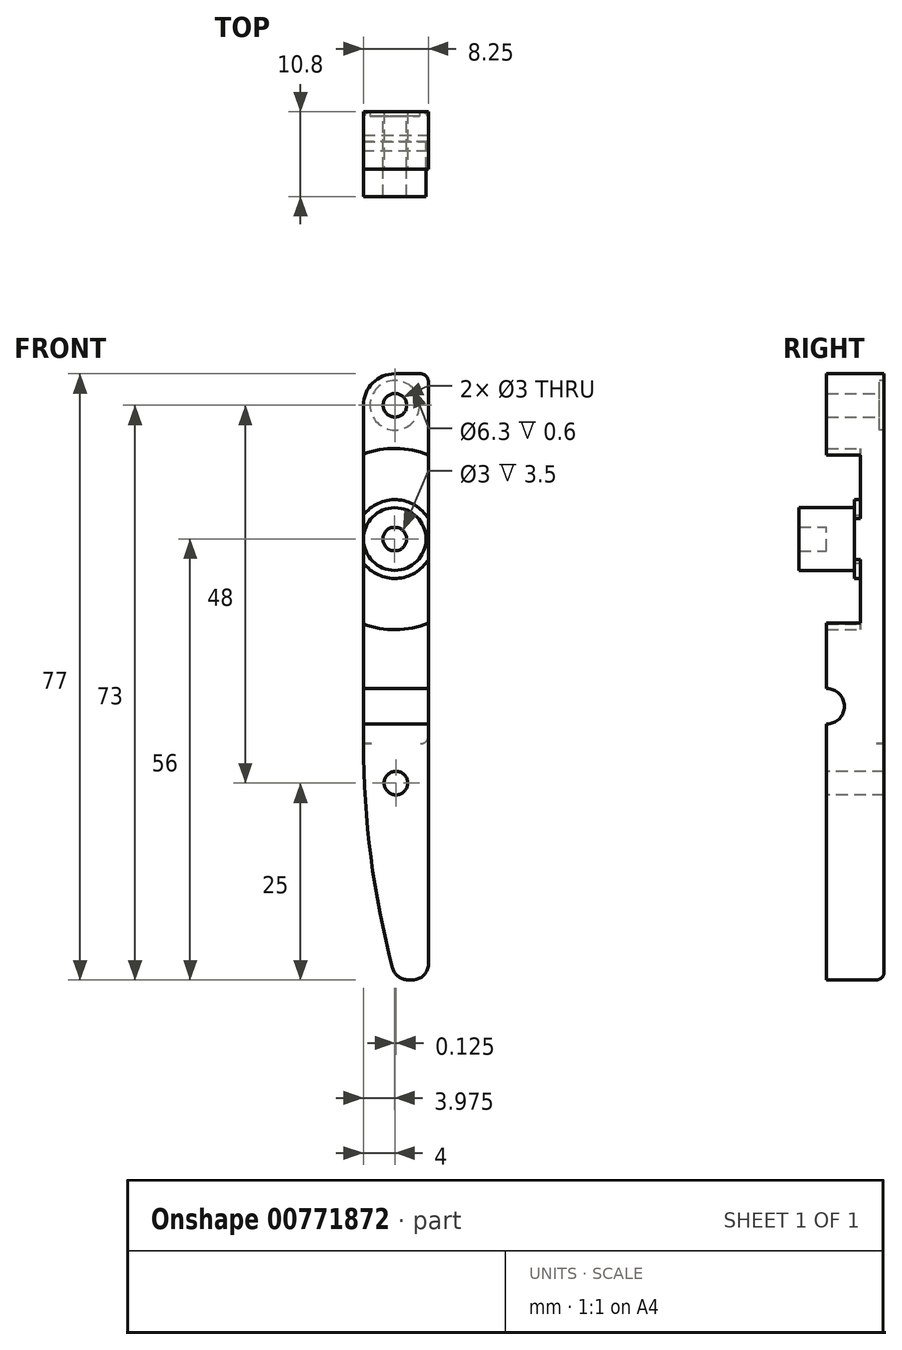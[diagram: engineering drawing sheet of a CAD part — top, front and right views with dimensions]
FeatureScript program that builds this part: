
annotation { "Feature Type Name" : "Feature", "Feature Type Description" : "" }
export const myFeature = defineFeature(function(context is Context, id is Id, definition is map)
    precondition{}
    {
        {
            var Q0;
            Q0=qCreatedBy(makeId("Front.planeOp"),FACE);
            var sketch = newSketch(context, id + "F0", { "sketchPlane" : qUnion([Q0])});
            skLineSegment(sketch, "E0.top", {"start": v(4, 47) * mm, "end": v(8.25, 47) * mm});
            skLineSegment(sketch, "E0.left", {"start": v(0, 0) * mm, "end": v(0, 43) * mm});
            skLineSegment(sketch, "E0.right", {"start": v(8.25, -28) * mm, "end": v(8.25, 47) * mm});
            skCircle(sketch, "E1", {"center": v(4, 43) * mm, "radius": 1.5 * mm});
            skPoint(sketch, "E2.visualSharp", {"position": v(0, 47) * mm});
            skArc(sketch, "E2.filletArc", {"start": v(4, 47) * mm, "mid": v(1.17, 45.83) * mm, "end": v(0, 43) * mm});
            skCircle(sketch, "E3", {"center": v(3.98, 26) * mm, "radius": 3.98 * mm});
            skArc(sketch, "E4", {"start": v(8.25, 28.6) * mm, "mid": v(4.24, 31) * mm, "end": v(0, 29.03) * mm});
            skArc(sketch, "E5.trimOffspring", {"start": v(0, 22.97) * mm, "mid": v(4.24, 21) * mm, "end": v(8.25, 23.4) * mm});
            skArc(sketch, "E6", {"start": v(0, 0) * mm, "mid": v(0.93, -14.38) * mm, "end": v(3.72, -28.51) * mm});
            skLineSegment(sketch, "E7", {"start": v(6.25, -30) * mm, "end": v(5.65, -30) * mm});
            skPoint(sketch, "E8.visualSharp", {"position": v(4.13, -30) * mm});
            skArc(sketch, "E8.filletArc", {"start": v(3.72, -28.51) * mm, "mid": v(4.43, -29.59) * mm, "end": v(5.65, -30) * mm});
            skPoint(sketch, "E9.visualSharp", {"position": v(8.25, -30) * mm});
            skArc(sketch, "E9.filletArc", {"start": v(6.25, -30) * mm, "mid": v(7.66, -29.41) * mm, "end": v(8.25, -28) * mm});
            skArc(sketch, "E10", {"start": v(8.25, 36.68) * mm, "mid": v(4.14, 37.5) * mm, "end": v(0, 36.8) * mm});
            skArc(sketch, "E11.trimOffspring", {"start": v(0, 15.2) * mm, "mid": v(4.14, 14.5) * mm, "end": v(8.25, 15.32) * mm});
            skLineSegment(sketch, "E12", {"start": v(8.25, 26) * mm, "end": v(7.95, 26) * mm});
            skCircle(sketch, "E13", {"center": v(3.98, 26) * mm, "radius": 1.5 * mm});
            skLineSegment(sketch, "E14", {"start": v(0, 0) * mm, "end": v(8.25, 0) * mm});
            skCircle(sketch, "E15", {"center": v(4.13, -5) * mm, "radius": 1.5 * mm});
            skPoint(sketch, "E16", {"position": v(4.13, 0) * mm});
            skCircle(sketch, "E17", {"center": v(4, 43) * mm, "radius": 3.15 * mm});
            skSolve(sketch);
        }
        {
            var Q0;
            Q0=qCreatedBy(makeId("Right.planeOp"),FACE);
            var sketch = newSketch(context, id + "F1", { "sketchPlane" : qUnion([Q0])});
            skCircle(sketch, "E18", {"center": v(-4.3, 4.75) * mm, "radius": 2.25 * mm});
            skSolve(sketch);
        }
        {
            var Q0;
            Q0=qCreatedBy(makeId("Top.planeOp"),FACE);
            var sketch = newSketch(context, id + "F2", { "sketchPlane" : qUnion([Q0])});
            skArc(sketch, "E19", {"start": v(8.25, 2) * mm, "mid": v(7.96, 2.7) * mm, "end": v(7.25, 3) * mm});
            skLineSegment(sketch, "E20", {"start": v(8.25, 2) * mm, "end": v(8.25, 3) * mm});
            skLineSegment(sketch, "E21", {"start": v(8.25, 3) * mm, "end": v(7.25, 3) * mm});
            skSolve(sketch);
        }
        {
            var Q0;
            Q0=makeQuery(id+"F0.imprint","IMPRINT",FACE,{"disambiguationData":[TD([[makeQuery(id+"F0.imprint","IMPRINT",EDGE,{"derivedFrom":sQuery(id+"F0.wireOp",EDGE,"E6")}),1.0]])]});
            extrude(context, id + "F3", {"entities" : qUnion([Q0]), "oppositeDirection" : true, "depth" : 3 * mm, "offsetDistance" : 25 * mm});
        }
        {
            var Q0;
            Q0=makeQuery(id+"F2.imprint","IMPRINT",FACE,{"disambiguationData":[TD([[makeQuery(id+"F2.imprint","IMPRINT",EDGE,{"derivedFrom":sQuery(id+"F2.wireOp",EDGE,"E19")}),-1.0]])]});
            var Q1;
            Q1=makeQuery(id+"F3.opExtrude","CAP_EDGE",EDGE,{"disambiguationData":[OSD([sQuery(id+"F0.wireOp",EDGE,"E6")])],"isStart":false});
            var Q2;
            Q2=makeQuery(id+"F3.opExtrude","CAP_EDGE",EDGE,{"disambiguationData":[OSD([sQuery(id+"F0.wireOp",EDGE,"E8.filletArc")])],"isStart":false});
            var Q3;
            Q3=makeQuery(id+"F3.opExtrude","CAP_EDGE",EDGE,{"disambiguationData":[OSD([sQuery(id+"F0.wireOp",EDGE,"E7")])],"isStart":false});
            var Q4;
            Q4=makeQuery(id+"F3.opExtrude","CAP_EDGE",EDGE,{"disambiguationData":[OSD([sQuery(id+"F0.wireOp",EDGE,"E9.filletArc")])],"isStart":false});
            var Q5;
            Q5=makeQuery(id+"F3.opExtrude","CAP_EDGE",EDGE,{"disambiguationData":[OSD([sQuery(id+"F0.wireOp",EDGE,"E0.right")])],"isStart":false});
            sweep(context, id + "F4", {"operationType" : NewBodyOperationType.REMOVE, "profiles" : qUnion([Q0]), "path" : qUnion([Q1, Q2, Q3, Q4, Q5])});
        }
        {
            var Q0;
            {var subQ2=sQuery(id+"F0.wireOp",EDGE,"E11.trimOffspring");Q0=makeQuery(id+"F0.imprint","IMPRINT",FACE,{"disambiguationData":[TD([[makeQuery(id+"F0.imprint","IMPRINT",EDGE,{"derivedFrom":subQ2}),-1.0]])]});}
            var Q1;
            {var subQ0=sQuery(id+"F0.wireOp",EDGE,"E5.trimOffspring");Q1=makeQuery(id+"F0.imprint","IMPRINT",FACE,{"disambiguationData":[TD([[makeQuery(id+"F0.imprint","IMPRINT",EDGE,{"derivedFrom":subQ0}),-1.0]])]});}
            var Q2;
            {var subQ0=sQuery(id+"F0.wireOp",EDGE,"E5.trimOffspring");Q2=makeQuery(id+"F0.imprint","IMPRINT",FACE,{"disambiguationData":[TD([[makeQuery(id+"F0.imprint","IMPRINT",EDGE,{"derivedFrom":subQ0}),1.0]])]});}
            var Q3;
            Q3=makeQuery(id+"F0.imprint","IMPRINT",FACE,{"disambiguationData":[TD([[makeQuery(id+"F0.imprint","IMPRINT",EDGE,{"derivedFrom":sQuery(id+"F0.wireOp",EDGE,"E13")}),-1.0]])]});
            var Q4;
            Q4=makeQuery(id+"F0.imprint","IMPRINT",FACE,{"disambiguationData":[TD([[makeQuery(id+"F0.imprint","IMPRINT",EDGE,{"derivedFrom":sQuery(id+"F0.wireOp",EDGE,"E13")}),1.0]])]});
            var Q5;
            {var subQ0=sQuery(id+"F0.wireOp",EDGE,"E4");Q5=makeQuery(id+"F0.imprint","IMPRINT",FACE,{"disambiguationData":[TD([[makeQuery(id+"F0.imprint","IMPRINT",EDGE,{"derivedFrom":subQ0}),1.0]])]});}
            var Q6;
            {var subQ0=sQuery(id+"F0.wireOp",EDGE,"E4");Q6=makeQuery(id+"F0.imprint","IMPRINT",FACE,{"disambiguationData":[TD([[makeQuery(id+"F0.imprint","IMPRINT",EDGE,{"derivedFrom":subQ0}),-1.0]])]});}
            var Q7;
            {var subQ1=sQuery(id+"F0.wireOp",EDGE,"E0.top");Q7=makeQuery(id+"F0.imprint","IMPRINT",FACE,{"disambiguationData":[TD([[makeQuery(id+"F0.imprint","IMPRINT",EDGE,{"derivedFrom":subQ1}),-1.0]])]});}
            var Q8;
            Q8=makeQuery(id+"F3.opExtrude","CAP_FACE",FACE,{"disambiguationData":[OSD([sQuery(id+"F0.wireOp",EDGE,"E0.right"),sQuery(id+"F0.wireOp",EDGE,"E6"),sQuery(id+"F0.wireOp",EDGE,"E7"),sQuery(id+"F0.wireOp",EDGE,"E8.filletArc"),sQuery(id+"F0.wireOp",EDGE,"E9.filletArc"),sQuery(id+"F0.wireOp",EDGE,"E14")])],"isStart":false});
            extrude(context, id + "F5", {"entities" : qUnion([Q0, Q1, Q2, Q3, Q4, Q5, Q6, Q7]), "operationType" : NewBodyOperationType.ADD, "endBound" : BoundingType.UP_TO_SURFACE, "oppositeDirection" : true, "depth" : 25 * mm, "endBoundEntityFace" : qUnion([Q8]), "offsetDistance" : 25 * mm});
        }
        {
            var Q0;
            {var subQ1=sQuery(id+"F0.wireOp",EDGE,"E0.top");Q0=makeQuery(id+"F0.imprint","IMPRINT",FACE,{"disambiguationData":[TD([[makeQuery(id+"F0.imprint","IMPRINT",EDGE,{"derivedFrom":subQ1}),-1.0]])]});}
            var Q1;
            {var subQ3=sQuery(id+"F0.wireOp",EDGE,"E6");Q1=makeQuery(id+"F0.imprint","IMPRINT",FACE,{"disambiguationData":[TD([[makeQuery(id+"F0.imprint","IMPRINT",EDGE,{"derivedFrom":subQ3}),1.0]])]});}
            var Q2;
            Q2=makeQuery(id+"F0.imprint","IMPRINT",FACE,{"disambiguationData":[TD([[makeQuery(id+"F0.imprint","IMPRINT",EDGE,{"derivedFrom":sQuery(id+"F0.wireOp",EDGE,"E13")}),1.0]])]});
            var Q3;
            {var subQ2=sQuery(id+"F0.wireOp",EDGE,"E11.trimOffspring");Q3=makeQuery(id+"F0.imprint","IMPRINT",FACE,{"disambiguationData":[TD([[makeQuery(id+"F0.imprint","IMPRINT",EDGE,{"derivedFrom":subQ2}),-1.0]])]});}
            var Q4;
            Q4=makeQuery(id+"F0.imprint","IMPRINT",FACE,{"disambiguationData":[TD([[makeQuery(id+"F0.imprint","IMPRINT",EDGE,{"derivedFrom":sQuery(id+"F0.wireOp",EDGE,"E1")}),-1.0]])]});
            extrude(context, id + "F6", {"entities" : qUnion([Q0, Q1, Q2, Q3, Q4]), "operationType" : NewBodyOperationType.ADD, "depth" : 4.3 * mm, "offsetDistance" : 25 * mm});
        }
        {
            var Q0;
            Q0=makeQuery(id+"F0.imprint","IMPRINT",FACE,{"disambiguationData":[TD([[makeQuery(id+"F0.imprint","IMPRINT",EDGE,{"derivedFrom":sQuery(id+"F0.wireOp",EDGE,"E3")}),1.0]])]});
            extrude(context, id + "F7", {"entities" : qUnion([Q0]), "operationType" : NewBodyOperationType.ADD, "depth" : 7.8 * mm, "offsetDistance" : 25 * mm});
        }
        {
            var Q0;
            {var subQ0=sQuery(id+"F0.wireOp",EDGE,"E4");Q0=makeQuery(id+"F0.imprint","IMPRINT",FACE,{"disambiguationData":[TD([[makeQuery(id+"F0.imprint","IMPRINT",EDGE,{"derivedFrom":subQ0}),1.0]])]});}
            extrude(context, id + "F8", {"entities" : qUnion([Q0]), "operationType" : NewBodyOperationType.ADD, "depth" : .8 * mm, "offsetDistance" : 25 * mm});
        }
        {
            var Q0;
            Q0=makeQuery(id+"F1.imprint","IMPRINT",FACE,{"disambiguationData":[TD([[makeQuery(id+"F1.imprint","IMPRINT",EDGE,{"derivedFrom":sQuery(id+"F1.wireOp",EDGE,"E18")}),1.0]])]});
            var Q1;
            {var subQ0=sQuery(id+"F0.wireOp",EDGE,"E0.right");Q1=makeQuery(id+"F10.boolean.opBoolean","MERGE",FACE,{"derivedFrom":[makeQuery(id+"F8.boolean.opBoolean","MERGE",FACE,{"derivedFrom":[makeQuery(id+"F6.boolean.opBoolean","MERGE",FACE,{"derivedFrom":[makeQuery(id+"F3.opExtrude","SWEPT_FACE",FACE,{"disambiguationData":[OSD([subQ0])]}),makeQuery(id+"F6.opExtrude","SWEPT_FACE",FACE,{"disambiguationData":[OSD([subQ0]),TDD([makeQuery(id+"F0.imprint","IMPRINT",EDGE,{"disambiguationData":[TD([[makeQuery(id+"F0.imprint","INTERSECT",VERTEX,{"derivedFrom":[subQ0,sQuery(id+"F0.wireOp",EDGE,"E9.filletArc")]}),-1.0]])],"derivedFrom":subQ0})])]}),makeQuery(id+"F6.opExtrude","SWEPT_FACE",FACE,{"disambiguationData":[OSD([subQ0]),TDD([makeQuery(id+"F0.imprint","IMPRINT",EDGE,{"disambiguationData":[TD([[makeQuery(id+"F0.imprint","INTERSECT",VERTEX,{"derivedFrom":[sQuery(id+"F0.wireOp",EDGE,"E0.top"),subQ0]}),1.0]])],"derivedFrom":subQ0})])]})]}),makeQuery(id+"F8.opExtrude","SWEPT_FACE",FACE,{"disambiguationData":[OSD([subQ0])]})]}),makeQuery(id+"F10.opExtrude","SWEPT_FACE",FACE,{"disambiguationData":[OSD([subQ0])]})]});}
            extrude(context, id + "F9", {"entities" : qUnion([Q0]), "operationType" : NewBodyOperationType.REMOVE, "endBound" : BoundingType.UP_TO_SURFACE, "depth" : 25 * mm, "endBoundEntityFace" : qUnion([Q1]), "offsetDistance" : 25 * mm});
        }
        {
            var Q0;
            {var subQ4=sQuery(id+"F0.wireOp",EDGE,"E5.trimOffspring");Q0=makeQuery(id+"F0.imprint","IMPRINT",FACE,{"disambiguationData":[TD([[makeQuery(id+"F0.imprint","IMPRINT",EDGE,{"derivedFrom":subQ4}),1.0]])]});}
            extrude(context, id + "F10", {"entities" : qUnion([Q0]), "operationType" : NewBodyOperationType.ADD, "depth" : .8 * mm, "offsetDistance" : 25 * mm});
        }
        {
            var Q0;
            Q0=makeQuery(id+"F2.imprint","IMPRINT",FACE,{"disambiguationData":[TD([[makeQuery(id+"F2.imprint","IMPRINT",EDGE,{"derivedFrom":sQuery(id+"F2.wireOp",EDGE,"E19")}),-1.0]])]});
            var Q1;
            Q1=sQuery(id+"F2.wireOp",EDGE,"E21");
            revolve(context, id + "F11", {"operationType" : NewBodyOperationType.REMOVE, "surfaceOperationType" : NewSurfaceOperationType.NEW, "entities" : qUnion([Q0]), "axis" : qUnion([Q1]), "revolveType" : RevolveType.FULL, "oppositeDirection" : true});
        }
        {
            var Q0;
            {var subQ0=sQuery(id+"F0.wireOp",EDGE,"E0.right");var subQ1=sQuery(id+"F0.wireOp",EDGE,"E0.top");Q0=makeQuery(id+"F6.boolean.opBoolean","MERGE",EDGE,{"derivedFrom":[makeQuery(id+"F5.opExtrude","SWEPT_EDGE",EDGE,{"disambiguationData":[OSD([subQ1,subQ0])]}),makeQuery(id+"F6.opExtrude","SWEPT_EDGE",EDGE,{"disambiguationData":[OSD([subQ1,subQ0])]})]});}
            fillet(context, id + "F12", {"entities" : qUnion([Q0]), "radius" : 1 * mm, "tangentPropagation" : true, "allowEdgeOverflow" : false});
        }
        {
            var Q0;
            Q0=makeQuery(id+"F0.imprint","IMPRINT",FACE,{"disambiguationData":[TD([[makeQuery(id+"F0.imprint","IMPRINT",EDGE,{"derivedFrom":sQuery(id+"F0.wireOp",EDGE,"E1")}),-1.0]])]});
            extrude(context, id + "F13", {"entities" : qUnion([Q0]), "operationType" : NewBodyOperationType.ADD, "oppositeDirection" : true, "depth" : 2.4 * mm, "offsetDistance" : 25 * mm});
        }
    });
